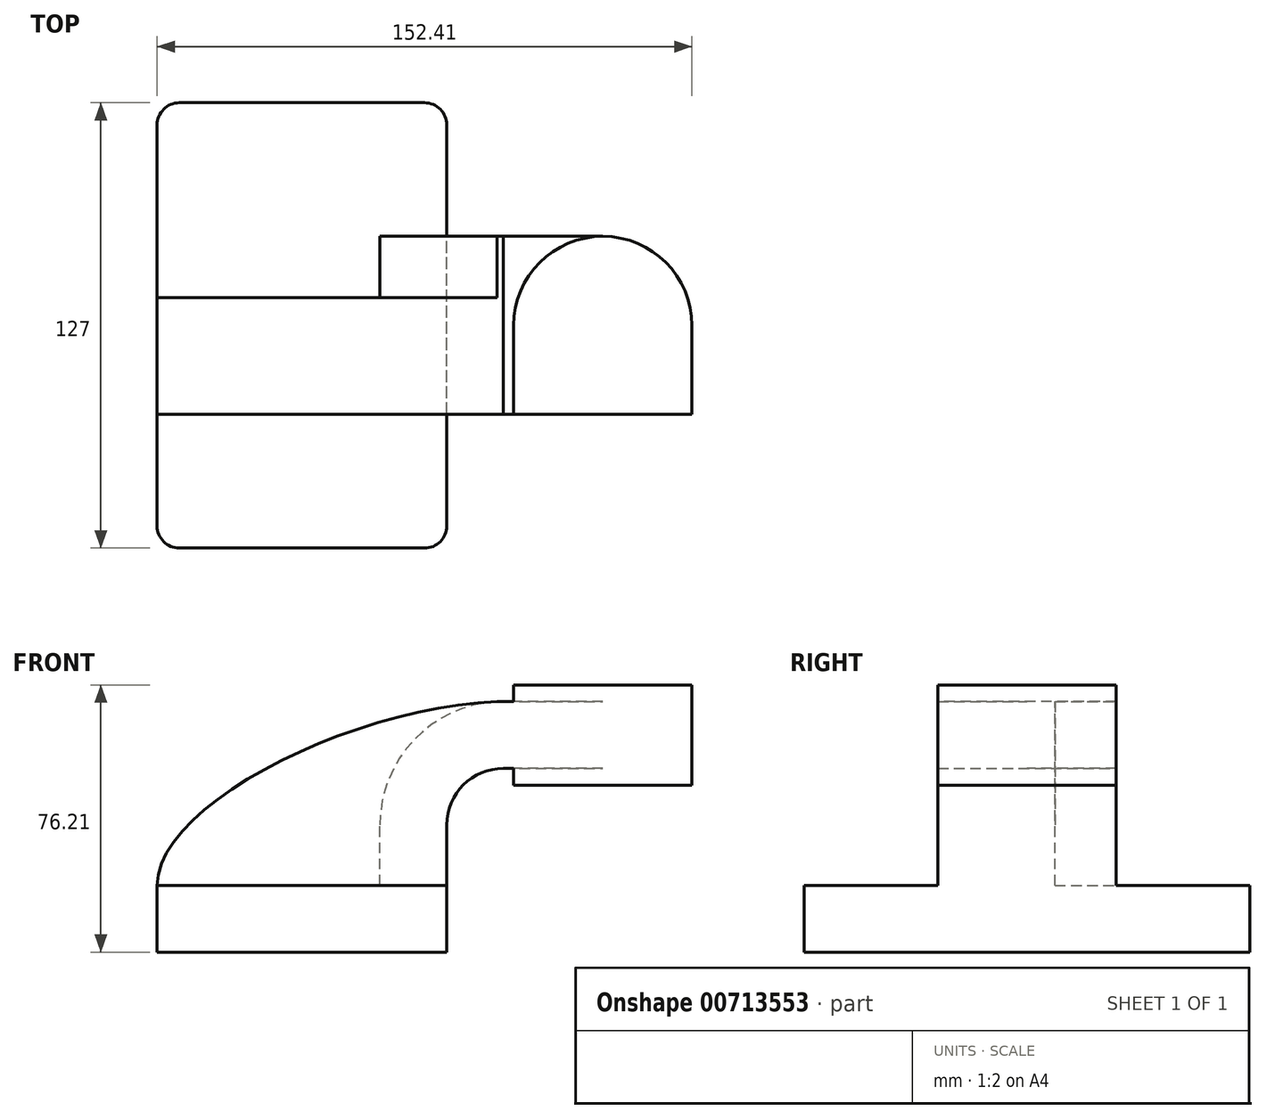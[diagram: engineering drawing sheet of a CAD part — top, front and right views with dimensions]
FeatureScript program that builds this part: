
annotation { "Feature Type Name" : "Feature", "Feature Type Description" : "" }
export const myFeature = defineFeature(function(context is Context, id is Id, definition is map)
    precondition{}
    {
        {
            var Q0;
            Q0=qCreatedBy(makeId("Front.planeOp"),FACE);
            var sketch = newSketch(context, id + "F0", { "sketchPlane" : qUnion([Q0])});
            skLineSegment(sketch, "E0.bottom", {"start": v(41.28, -9.52) * mm, "end": v(-41.28, -9.52) * mm});
            skLineSegment(sketch, "E0.top", {"start": v(41.28, 9.53) * mm, "end": v(-41.28, 9.53) * mm});
            skLineSegment(sketch, "E0.left", {"start": v(41.28, -9.52) * mm, "end": v(41.28, 9.53) * mm});
            skLineSegment(sketch, "E0.right", {"start": v(-41.28, -9.52) * mm, "end": v(-41.28, 9.53) * mm});
            skPoint(sketch, "E0.middle", {"position": v(0, 0) * mm});
            skLineSegment(sketch, "E1.bottom", {"start": v(111.12, 38.1) * mm, "end": v(60.33, 38.1) * mm});
            skLineSegment(sketch, "E1.top", {"start": v(111.12, 66.68) * mm, "end": v(60.33, 66.68) * mm});
            skLineSegment(sketch, "E1.left", {"start": v(111.12, 38.1) * mm, "end": v(111.12, 66.68) * mm});
            skLineSegment(sketch, "E1.right", {"start": v(60.33, 38.1) * mm, "end": v(60.33, 66.68) * mm});
            skPoint(sketch, "E1.middle", {"position": v(85.72, 52.39) * mm});
            skLineSegment(sketch, "E2", {"start": v(41.28, 9.53) * mm, "end": v(41.28, 26.75) * mm});
            skArc(sketch, "E3", {"start": v(41.27, 26.75) * mm, "mid": v(46, 38.15) * mm, "end": v(57.4, 42.88) * mm});
            skLineSegment(sketch, "E4", {"start": v(57.4, 42.88) * mm, "end": v(85.72, 42.88) * mm});
            skLineSegment(sketch, "E5.0", {"start": v(57.4, 61.93) * mm, "end": v(85.72, 61.93) * mm});
            skArc(sketch, "E5.1", {"start": v(22.22, 26.75) * mm, "mid": v(32.53, 51.62) * mm, "end": v(57.4, 61.93) * mm});
            skLineSegment(sketch, "E5.2", {"start": v(22.23, 9.53) * mm, "end": v(22.23, 26.75) * mm});
            skLineSegment(sketch, "E6", {"start": v(85.72, 66.68) * mm, "end": v(85.72, 38.1) * mm});
            skFitSpline(sketch, "E7", {"points": [v(-41.28, 9.53) * mm, v(57.4, 61.93) * mm], "startDerivative": vector(-0.13, 70.46) * mm, "endDerivative": vector(123.87, 2.07) * mm});
            skSolve(sketch);
        }
        {
            var Q0;
            Q0=makeQuery(id+"F0.imprint","IMPRINT",FACE,{"disambiguationData":[TD([[makeQuery(id+"F0.imprint","IMPRINT",EDGE,{"derivedFrom":sQuery(id+"F0.wireOp",EDGE,"E0.bottom")}),-1.0]])]});
            extrude(context, id + "F1", {"entities" : qUnion([Q0]), "endBound" : BoundingType.SYMMETRIC, "depth" : 127 * mm, "offsetDistance" : 25.4 * mm});
        }
        {
            var Q0;
            {var subQ1=sQuery(id+"F0.wireOp",EDGE,"E2");Q0=makeQuery(id+"F0.imprint","IMPRINT",FACE,{"disambiguationData":[TD([[makeQuery(id+"F0.imprint","IMPRINT",EDGE,{"derivedFrom":subQ1}),1.0]])]});}
            var Q1;
            {var subQ0=sQuery(id+"F0.wireOp",EDGE,"E4");var subQ1=sQuery(id+"F0.wireOp",EDGE,"E1.right");var subQ2=makeQuery(id+"F0.imprint","INTERSECT",VERTEX,{"derivedFrom":[subQ1,subQ0]});Q1=makeQuery(id+"F0.imprint","IMPRINT",FACE,{"disambiguationData":[TD([[makeQuery(id+"F0.imprint","IMPRINT",EDGE,{"disambiguationData":[TD([[subQ2,-1.0]])],"derivedFrom":subQ1}),-1.0]])]});}
            extrude(context, id + "F2", {"entities" : qUnion([Q0, Q1]), "operationType" : NewBodyOperationType.ADD, "endBound" : BoundingType.SYMMETRIC, "depth" : 50.8 * mm, "offsetDistance" : 25.4 * mm});
        }
        {
            var Q0;
            {var subQ3=sQuery(id+"F0.wireOp",EDGE,"E5.2");Q0=makeQuery(id+"F0.imprint","IMPRINT",FACE,{"disambiguationData":[TD([[makeQuery(id+"F0.imprint","IMPRINT",EDGE,{"derivedFrom":subQ3}),1.0]])]});}
            extrude(context, id + "F3", {"entities" : qUnion([Q0]), "operationType" : NewBodyOperationType.ADD, "endBound" : BoundingType.SYMMETRIC, "depth" : 15.88 * mm, "offsetDistance" : 25.4 * mm});
        }
        {
            var Q0;
            {var subQ0=sQuery(id+"F0.wireOp",EDGE,"E1.left");Q0=makeQuery(id+"F0.imprint","IMPRINT",FACE,{"disambiguationData":[TD([[makeQuery(id+"F0.imprint","IMPRINT",EDGE,{"derivedFrom":subQ0}),1.0]])]});}
            var Q1;
            Q1=sQuery(id+"F0.wireOp",EDGE,"E6");
            revolve(context, id + "F4", {"operationType" : NewBodyOperationType.ADD, "surfaceOperationType" : NewSurfaceOperationType.NEW, "entities" : qUnion([Q0]), "axis" : qUnion([Q1]), "revolveType" : RevolveType.FULL});
        }
        {
            var Q0;
            Q0=makeQuery(id+"F1.opExtrude","CAP_EDGE",EDGE,{"disambiguationData":[OSD([sQuery(id+"F0.wireOp",EDGE,"E0.right")])],"isStart":false});
            var Q1;
            Q1=makeQuery(id+"F1.opExtrude","CAP_EDGE",EDGE,{"disambiguationData":[OSD([sQuery(id+"F0.wireOp",EDGE,"E0.left")])],"isStart":false});
            var Q2;
            Q2=makeQuery(id+"F1.opExtrude","CAP_EDGE",EDGE,{"disambiguationData":[OSD([sQuery(id+"F0.wireOp",EDGE,"E0.right")])],"isStart":true});
            var Q3;
            Q3=makeQuery(id+"F1.opExtrude","CAP_EDGE",EDGE,{"disambiguationData":[OSD([sQuery(id+"F0.wireOp",EDGE,"E0.left")])],"isStart":true});
            fillet(context, id + "F5", {"entities" : qUnion([Q0, Q1, Q2, Q3]), "radius" : 6.35 * mm, "tangentPropagation" : true, "allowEdgeOverflow" : false});
        }
        {
            var Q0;
            Q0 = qSketchRegion(id + "F0", true);
            extrude(context, id + "F6", {"entities" : qUnion([Q0]), "operationType" : NewBodyOperationType.ADD, "depth" : 25.4 * mm, "offsetDistance" : 25.4 * mm});
        }
    });
